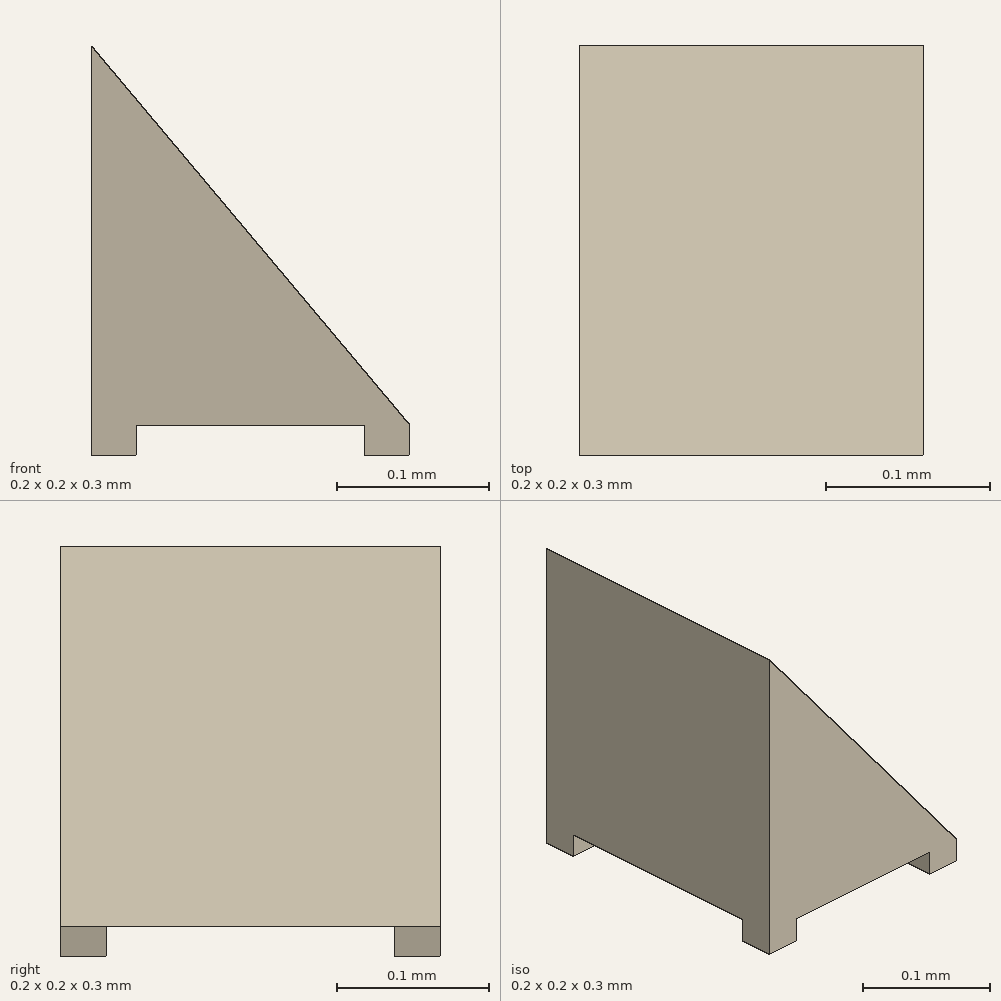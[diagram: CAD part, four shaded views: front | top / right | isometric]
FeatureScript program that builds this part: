
annotation { "Feature Type Name" : "Feature", "Feature Type Description" : "" }
export const myFeature = defineFeature(function(context is Context, id is Id, definition is map)
    precondition{}
    {
        {
            var Q0;
            Q0=qCreatedBy(makeId("Front.planeOp"),FACE);
            var sketch = newSketch(context, id + "F0", { "sketchPlane" : qUnion([Q0])});
            skLineSegment(sketch, "E0", {"start": v(0, 0) * mm, "end": v(0, 0.25) * mm});
            skLineSegment(sketch, "E1", {"start": v(0, 0.25) * mm, "end": v(0.21, 0) * mm});
            skLineSegment(sketch, "E2", {"start": v(0.21, 0) * mm, "end": v(0, 0) * mm});
            skSolve(sketch);
        }
        {
            var Q0;
            Q0=makeQuery(id+"F0.imprint","IMPRINT",FACE,{"disambiguationData":[TD([[makeQuery(id+"F0.imprint","IMPRINT",EDGE,{"derivedFrom":sQuery(id+"F0.wireOp",EDGE,"E0")}),-1.0]])]});
            extrude(context, id + "F1", {"entities" : qUnion([Q0]), "depth" : 0.25 * mm});
        }
        {
            var Q0;
            Q0=makeQuery(id+"F1.opExtrude","SWEPT_FACE",FACE,{"disambiguationData":[OSD([sQuery(id+"F0.wireOp",EDGE,"E2")])]});
            var sketch = newSketch(context, id + "F2", { "sketchPlane" : qUnion([Q0])});
            skLineSegment(sketch, "E3.bottom", {"start": v(0.21, 0) * mm, "end": v(0.18, 0) * mm});
            skLineSegment(sketch, "E3.top", {"start": v(0.21, 0.03) * mm, "end": v(0.18, 0.03) * mm});
            skLineSegment(sketch, "E3.left", {"start": v(0.21, 0) * mm, "end": v(0.21, 0.03) * mm});
            skLineSegment(sketch, "E3.right", {"start": v(0.18, 0) * mm, "end": v(0.18, 0.03) * mm});
            skLineSegment(sketch, "E4.bottom", {"start": v(0, 0) * mm, "end": v(0.03, 0) * mm});
            skLineSegment(sketch, "E4.top", {"start": v(0, 0.03) * mm, "end": v(0.03, 0.03) * mm});
            skLineSegment(sketch, "E4.left", {"start": v(0, 0) * mm, "end": v(0, 0.03) * mm});
            skLineSegment(sketch, "E4.right", {"start": v(0.03, 0) * mm, "end": v(0.03, 0.03) * mm});
            skLineSegment(sketch, "E5.bottom", {"start": v(0.21, 0.25) * mm, "end": v(0.18, 0.25) * mm});
            skLineSegment(sketch, "E5.top", {"start": v(0.2, 0.22) * mm, "end": v(0.18, 0.22) * mm});
            skLineSegment(sketch, "E5.left", {"start": v(0.21, 0.25) * mm, "end": v(0.21, 0.22) * mm});
            skLineSegment(sketch, "E5.right", {"start": v(0.18, 0.25) * mm, "end": v(0.18, 0.22) * mm});
            skLineSegment(sketch, "E6.bottom", {"start": v(0, 0.25) * mm, "end": v(0.03, 0.25) * mm});
            skLineSegment(sketch, "E6.top", {"start": v(0, 0.22) * mm, "end": v(0.03, 0.22) * mm});
            skLineSegment(sketch, "E6.left", {"start": v(0, 0.25) * mm, "end": v(0, 0.22) * mm});
            skLineSegment(sketch, "E6.right", {"start": v(0.03, 0.25) * mm, "end": v(0.03, 0.22) * mm});
            skSolve(sketch);
        }
        {
            var Q0;
            Q0=makeQuery(id+"F2.imprint","IMPRINT",FACE,{"disambiguationData":[TD([[makeQuery(id+"F2.imprint","IMPRINT",EDGE,{"derivedFrom":sQuery(id+"F2.wireOp",EDGE,"E3.bottom")}),-1.0]])]});
            var Q1;
            Q1=makeQuery(id+"F2.imprint","IMPRINT",FACE,{"disambiguationData":[TD([[makeQuery(id+"F2.imprint","IMPRINT",EDGE,{"derivedFrom":sQuery(id+"F2.wireOp",EDGE,"E4.bottom")}),-1.0]])]});
            var Q2;
            Q2=makeQuery(id+"F2.imprint","IMPRINT",FACE,{"disambiguationData":[TD([[makeQuery(id+"F2.imprint","IMPRINT",EDGE,{"derivedFrom":sQuery(id+"F2.wireOp",EDGE,"E6.bottom")}),1.0]])]});
            var Q3;
            Q3=makeQuery(id+"F2.imprint","IMPRINT",FACE,{"disambiguationData":[TD([[makeQuery(id+"F2.imprint","IMPRINT",EDGE,{"derivedFrom":sQuery(id+"F2.wireOp",EDGE,"E5.bottom")}),1.0]])]});
            extrude(context, id + "F3", {"entities" : qUnion([Q0, Q1, Q2, Q3]), "operationType" : NewBodyOperationType.ADD, "depth" : 0.02 * mm});
        }
    });
